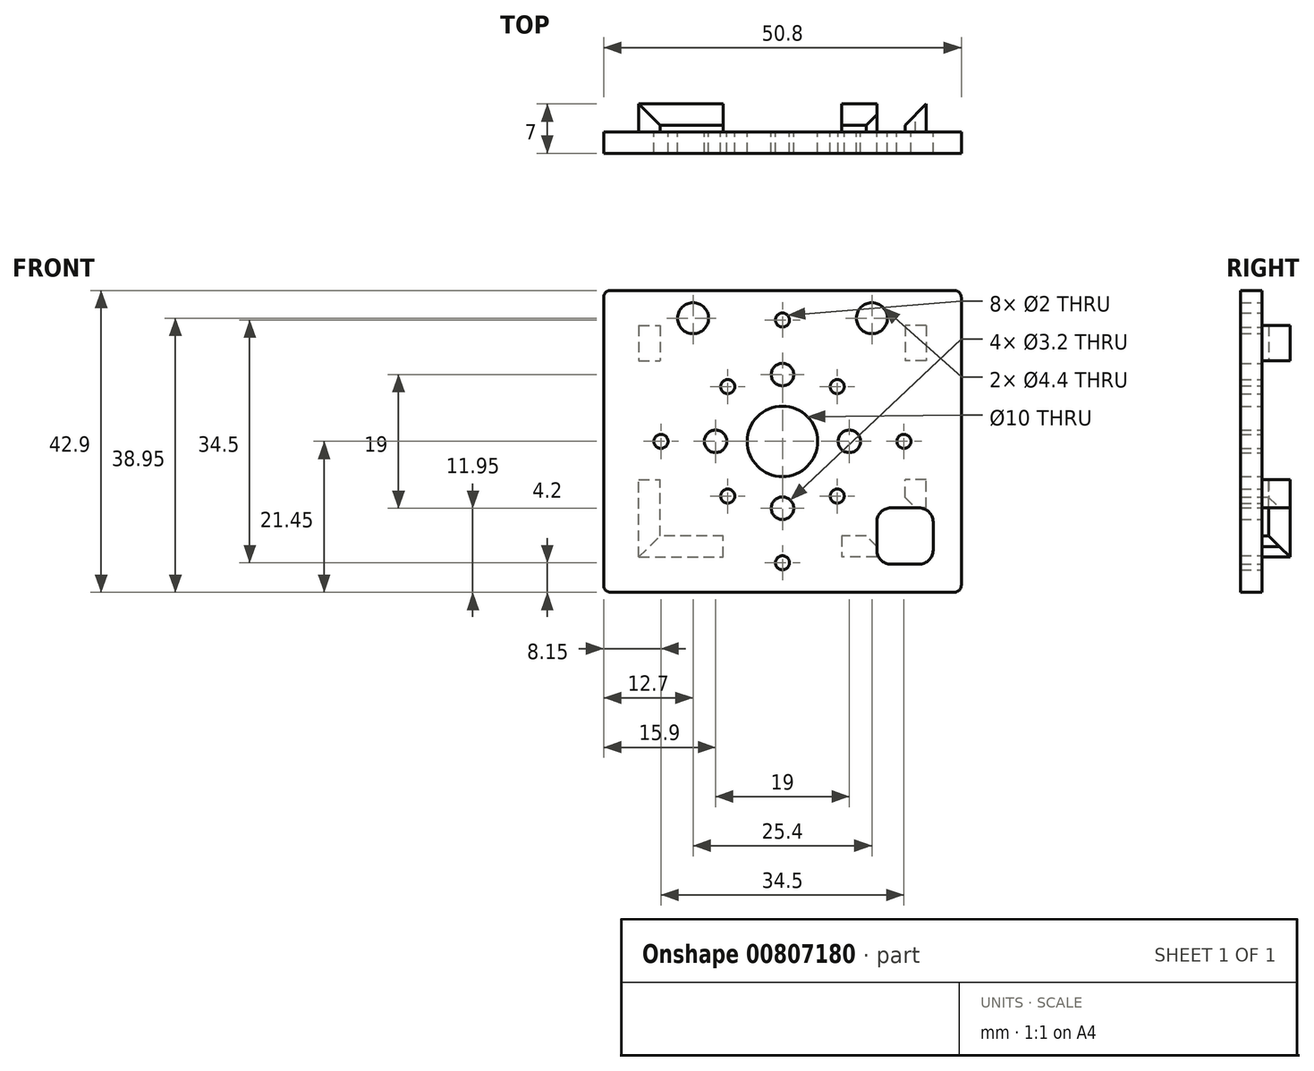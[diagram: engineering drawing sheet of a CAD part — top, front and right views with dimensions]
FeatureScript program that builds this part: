
annotation { "Feature Type Name" : "Feature", "Feature Type Description" : "" }
export const myFeature = defineFeature(function(context is Context, id is Id, definition is map)
    precondition{}
    {
        {
            var Q0;
            Q0=qCreatedBy(makeId("Front.planeOp"),FACE);
            var sketch = newSketch(context, id + "F0", { "sketchPlane" : qUnion([Q0])});
            skLineSegment(sketch, "E0.bottom", {"start": v(25.4, 21.45) * mm, "end": v(-25.4, 21.45) * mm});
            skLineSegment(sketch, "E0.top", {"start": v(25.4, -21.45) * mm, "end": v(-25.4, -21.45) * mm});
            skLineSegment(sketch, "E0.left", {"start": v(25.4, 21.45) * mm, "end": v(25.4, -21.45) * mm});
            skLineSegment(sketch, "E0.right", {"start": v(-25.4, 21.45) * mm, "end": v(-25.4, -21.45) * mm});
            skPoint(sketch, "E0.middle", {"position": v(0, 0) * mm});
            skCircle(sketch, "E1", {"center": v(0, 0) * mm, "radius": 5 * mm});
            skLineSegment(sketch, "E2.bottom", {"start": v(19.4, -17.45) * mm, "end": v(15.4, -17.45) * mm});
            skLineSegment(sketch, "E2.top", {"start": v(19.4, -9.45) * mm, "end": v(15.4, -9.45) * mm});
            skLineSegment(sketch, "E2.left", {"start": v(21.4, -15.45) * mm, "end": v(21.4, -11.45) * mm});
            skLineSegment(sketch, "E2.right", {"start": v(13.4, -15.45) * mm, "end": v(13.4, -11.45) * mm});
            skPoint(sketch, "E3.visualSharp", {"position": v(13.4, -9.45) * mm});
            skArc(sketch, "E3.filletArc", {"start": v(15.4, -9.45) * mm, "mid": v(13.99, -10.04) * mm, "end": v(13.4, -11.45) * mm});
            skPoint(sketch, "E4.visualSharp", {"position": v(21.4, -9.45) * mm});
            skArc(sketch, "E4.filletArc", {"start": v(21.4, -11.45) * mm, "mid": v(20.81, -10.04) * mm, "end": v(19.4, -9.45) * mm});
            skPoint(sketch, "E5.visualSharp", {"position": v(21.4, -17.45) * mm});
            skArc(sketch, "E5.filletArc", {"start": v(19.4, -17.45) * mm, "mid": v(20.81, -16.86) * mm, "end": v(21.4, -15.45) * mm});
            skPoint(sketch, "E6.visualSharp", {"position": v(13.4, -17.45) * mm});
            skArc(sketch, "E6.filletArc", {"start": v(13.4, -15.45) * mm, "mid": v(13.99, -16.86) * mm, "end": v(15.4, -17.45) * mm});
            skCircle(sketch, "E7", {"center": v(0, 17.25) * mm, "radius": 1 * mm});
            skCircle(sketch, "E8", {"center": v(7.78, 7.78) * mm, "radius": 1 * mm});
            skLineSegment(sketch, "E9", {"start": v(0, 0) * mm, "end": v(0, 17.25) * mm, "construction": true});
            skLineSegment(sketch, "E10", {"start": v(0, 0) * mm, "end": v(7.78, 7.78) * mm, "construction": true});
            skCircle(sketch, "E11", {"center": v(-12.7, 17.5) * mm, "radius": 2.2 * mm});
            skCircle(sketch, "E12.MirrorC", {"center": v(12.7, 17.5) * mm, "radius": 2.2 * mm});
            skCircle(sketch, "E13.1.0", {"center": v(-17.25, 0) * mm, "radius": 1 * mm});
            skCircle(sketch, "E13.1.1", {"center": v(-7.78, 7.78) * mm, "radius": 1 * mm});
            skCircle(sketch, "E13.2.0", {"center": v(0, -17.25) * mm, "radius": 1 * mm});
            skCircle(sketch, "E13.2.1", {"center": v(-7.78, -7.78) * mm, "radius": 1 * mm});
            skCircle(sketch, "E13.3.0", {"center": v(17.25, 0) * mm, "radius": 1 * mm});
            skCircle(sketch, "E13.3.1", {"center": v(7.78, -7.78) * mm, "radius": 1 * mm});
            skCircle(sketch, "E14", {"center": v(0, 0) * mm, "radius": 17.25 * mm, "construction": true});
            skCircle(sketch, "E15", {"center": v(0, 0) * mm, "radius": 11 * mm, "construction": true});
            skCircle(sketch, "E16", {"center": v(0, 0) * mm, "radius": 9.5 * mm, "construction": true});
            skCircle(sketch, "E17", {"center": v(9.5, 0) * mm, "radius": 1.6 * mm});
            skCircle(sketch, "E18.1.0", {"center": v(0, 9.5) * mm, "radius": 1.6 * mm});
            skCircle(sketch, "E18.2.0", {"center": v(-9.5, 0) * mm, "radius": 1.6 * mm});
            skCircle(sketch, "E18.3.0", {"center": v(0, -9.5) * mm, "radius": 1.6 * mm});
            skSolve(sketch);
        }
        {
            var Q0;
            Q0=makeQuery(id+"F0.imprint","IMPRINT",FACE,{"disambiguationData":[TD([[makeQuery(id+"F0.imprint","IMPRINT",EDGE,{"derivedFrom":sQuery(id+"F0.wireOp",EDGE,"E0.bottom")}),1.0]])]});
            extrude(context, id + "F1", {"entities" : qUnion([Q0]), "depth" : 3 * mm});
        }
        {
            var Q0;
            Q0=makeQuery(id+"F1.opExtrude","SWEPT_EDGE",EDGE,{"disambiguationData":[OSD([sQuery(id+"F0.wireOp",EDGE,"E0.bottom"),sQuery(id+"F0.wireOp",EDGE,"E0.left")])]});
            var Q1;
            Q1=makeQuery(id+"F1.opExtrude","SWEPT_EDGE",EDGE,{"disambiguationData":[OSD([sQuery(id+"F0.wireOp",EDGE,"E0.top"),sQuery(id+"F0.wireOp",EDGE,"E0.left")])]});
            var Q2;
            Q2=makeQuery(id+"F1.opExtrude","SWEPT_EDGE",EDGE,{"disambiguationData":[OSD([sQuery(id+"F0.wireOp",EDGE,"E0.top"),sQuery(id+"F0.wireOp",EDGE,"E0.right")])]});
            var Q3;
            Q3=makeQuery(id+"F1.opExtrude","SWEPT_EDGE",EDGE,{"disambiguationData":[OSD([sQuery(id+"F0.wireOp",EDGE,"E0.bottom"),sQuery(id+"F0.wireOp",EDGE,"E0.right")])]});
            fillet(context, id + "F2", {"entities" : qUnion([Q0, Q1, Q2, Q3]), "radius" : 1 * mm, "tangentPropagation" : true, "allowEdgeOverflow" : false});
        }
        {
            var Q0;
            Q0=makeQuery(id+"F1.opExtrude","CAP_FACE",FACE,{"disambiguationData":[OSD([sQuery(id+"F0.wireOp",EDGE,"E0.bottom"),sQuery(id+"F0.wireOp",EDGE,"E0.top"),sQuery(id+"F0.wireOp",EDGE,"E0.left"),sQuery(id+"F0.wireOp",EDGE,"E0.right"),sQuery(id+"F0.wireOp",EDGE,"E1"),sQuery(id+"F0.wireOp",EDGE,"E2.bottom"),sQuery(id+"F0.wireOp",EDGE,"E2.top"),sQuery(id+"F0.wireOp",EDGE,"E2.left"),sQuery(id+"F0.wireOp",EDGE,"E2.right"),sQuery(id+"F0.wireOp",EDGE,"E3.filletArc"),sQuery(id+"F0.wireOp",EDGE,"E4.filletArc"),sQuery(id+"F0.wireOp",EDGE,"E5.filletArc"),sQuery(id+"F0.wireOp",EDGE,"E6.filletArc"),sQuery(id+"F0.wireOp",EDGE,"E7"),sQuery(id+"F0.wireOp",EDGE,"E8"),sQuery(id+"F0.wireOp",EDGE,"E11"),sQuery(id+"F0.wireOp",EDGE,"E12.MirrorC"),sQuery(id+"F0.wireOp",EDGE,"E13.1.0"),sQuery(id+"F0.wireOp",EDGE,"E13.1.1"),sQuery(id+"F0.wireOp",EDGE,"E13.2.0"),sQuery(id+"F0.wireOp",EDGE,"E13.2.1"),sQuery(id+"F0.wireOp",EDGE,"E13.3.0"),sQuery(id+"F0.wireOp",EDGE,"E13.3.1")])],"isStart":true});
            var sketch = newSketch(context, id + "F3", { "sketchPlane" : qUnion([Q0])});
            skLineSegment(sketch, "E19.bottom", {"start": v(-20.4, 16.45) * mm, "end": v(-17.4, 16.45) * mm});
            skLineSegment(sketch, "E19.top", {"start": v(-20.4, 11.45) * mm, "end": v(-17.4, 11.45) * mm});
            skLineSegment(sketch, "E19.left", {"start": v(-20.4, 16.45) * mm, "end": v(-20.4, 11.45) * mm});
            skLineSegment(sketch, "E19.right", {"start": v(-17.4, 16.45) * mm, "end": v(-17.4, 11.45) * mm});
            skLineSegment(sketch, "E20.bottom", {"start": v(-20.4, -5.45) * mm, "end": v(-17.4, -5.45) * mm});
            skLineSegment(sketch, "E20.top", {"start": v(-20.4, -9.45) * mm, "end": v(-17.4, -9.45) * mm});
            skLineSegment(sketch, "E20.left", {"start": v(-20.4, -9.45) * mm, "end": v(-20.4, -5.45) * mm});
            skLineSegment(sketch, "E20.right", {"start": v(-17.4, -9.45) * mm, "end": v(-17.4, -5.45) * mm});
            skLineSegment(sketch, "E21.MirrorCS", {"start": v(20.4, 16.45) * mm, "end": v(17.4, 16.45) * mm});
            skLineSegment(sketch, "E22.MirrorCS", {"start": v(20.4, 11.45) * mm, "end": v(17.4, 11.45) * mm});
            skLineSegment(sketch, "E23.MirrorCS", {"start": v(17.4, 16.45) * mm, "end": v(17.4, 11.45) * mm});
            skLineSegment(sketch, "E24.MirrorCS", {"start": v(20.4, 16.45) * mm, "end": v(20.4, 11.45) * mm});
            skLineSegment(sketch, "E25.top", {"start": v(20.4, -5.45) * mm, "end": v(17.4, -5.45) * mm});
            skLineSegment(sketch, "E25.left", {"start": v(20.4, -16.45) * mm, "end": v(20.4, -5.45) * mm});
            skLineSegment(sketch, "E25.right", {"start": v(17.4, -13.45) * mm, "end": v(17.4, -5.45) * mm});
            skLineSegment(sketch, "E26", {"start": v(20.4, -16.45) * mm, "end": v(8.4, -16.45) * mm});
            skLineSegment(sketch, "E27", {"start": v(8.4, -16.45) * mm, "end": v(8.4, -13.45) * mm});
            skLineSegment(sketch, "E28", {"start": v(8.4, -13.45) * mm, "end": v(17.4, -13.45) * mm});
            skLineSegment(sketch, "E29.bottom", {"start": v(-13.4, -13.45) * mm, "end": v(-8.4, -13.45) * mm});
            skLineSegment(sketch, "E29.top", {"start": v(-13.4, -16.45) * mm, "end": v(-8.4, -16.45) * mm});
            skLineSegment(sketch, "E29.left", {"start": v(-13.4, -13.45) * mm, "end": v(-13.4, -16.45) * mm});
            skLineSegment(sketch, "E29.right", {"start": v(-8.4, -13.45) * mm, "end": v(-8.4, -16.45) * mm});
            skSolve(sketch);
        }
        {
            var Q0;
            Q0=qSketchRegion(id+"F3",true);
            extrude(context, id + "F4", {"entities" : qUnion([Q0]), "operationType" : NewBodyOperationType.ADD, "depth" : 4 * mm});
        }
        {
            var Q0;
            Q0=makeQuery(id+"F4.opExtrude","SWEPT_EDGE",EDGE,{"disambiguationData":[OSD([sQuery(id+"F0.wireOp",EDGE,"E2.right"),sQuery(id+"F3.wireOp",EDGE,"E29.bottom"),sQuery(id+"F3.wireOp",EDGE,"E29.left")])]});
            var Q1;
            Q1=makeQuery(id+"F4.opExtrude","SWEPT_EDGE",EDGE,{"disambiguationData":[OSD([sQuery(id+"F0.wireOp",EDGE,"E2.top"),sQuery(id+"F3.wireOp",EDGE,"E20.top"),sQuery(id+"F3.wireOp",EDGE,"E20.right")])]});
            chamfer(context, id + "F5", {"entities" : qUnion([Q0, Q1]), "width" : 1.5 * mm, "tangentPropagation" : true});
        }
        {
            var Q0;
            Q0=makeQuery(id+"F4.opExtrude","CAP_EDGE",EDGE,{"disambiguationData":[OSD([sQuery(id+"F3.wireOp",EDGE,"E19.right")])],"isStart":false});
            chamfer(context, id + "F6", {"entities" : qUnion([Q0]), "width" : 3 * mm, "tangentPropagation" : true});
        }
        {
            var Q0;
            Q0=makeQuery(id+"F4.opExtrude","CAP_EDGE",EDGE,{"disambiguationData":[OSD([sQuery(id+"F3.wireOp",EDGE,"E23.MirrorCS")])],"isStart":false});
            var Q1;
            Q1=makeQuery(id+"F4.opExtrude","CAP_EDGE",EDGE,{"disambiguationData":[OSD([sQuery(id+"F3.wireOp",EDGE,"E25.right")])],"isStart":false});
            var Q2;
            Q2=makeQuery(id+"F4.opExtrude","CAP_EDGE",EDGE,{"disambiguationData":[OSD([sQuery(id+"F3.wireOp",EDGE,"E28")])],"isStart":false});
            var Q3;
            Q3=makeQuery(id+"F4.opExtrude","CAP_EDGE",EDGE,{"disambiguationData":[OSD([sQuery(id+"F3.wireOp",EDGE,"E29.bottom")])],"isStart":false});
            var Q4;
            Q4=makeQuery(id+"F4.opExtrude","CAP_EDGE",EDGE,{"disambiguationData":[OSD([sQuery(id+"F3.wireOp",EDGE,"E20.right")])],"isStart":false});
            chamfer(context, id + "F7", {"entities" : qUnion([Q0, Q1, Q2, Q3, Q4]), "width" : 3 * mm, "tangentPropagation" : true});
        }
    });
